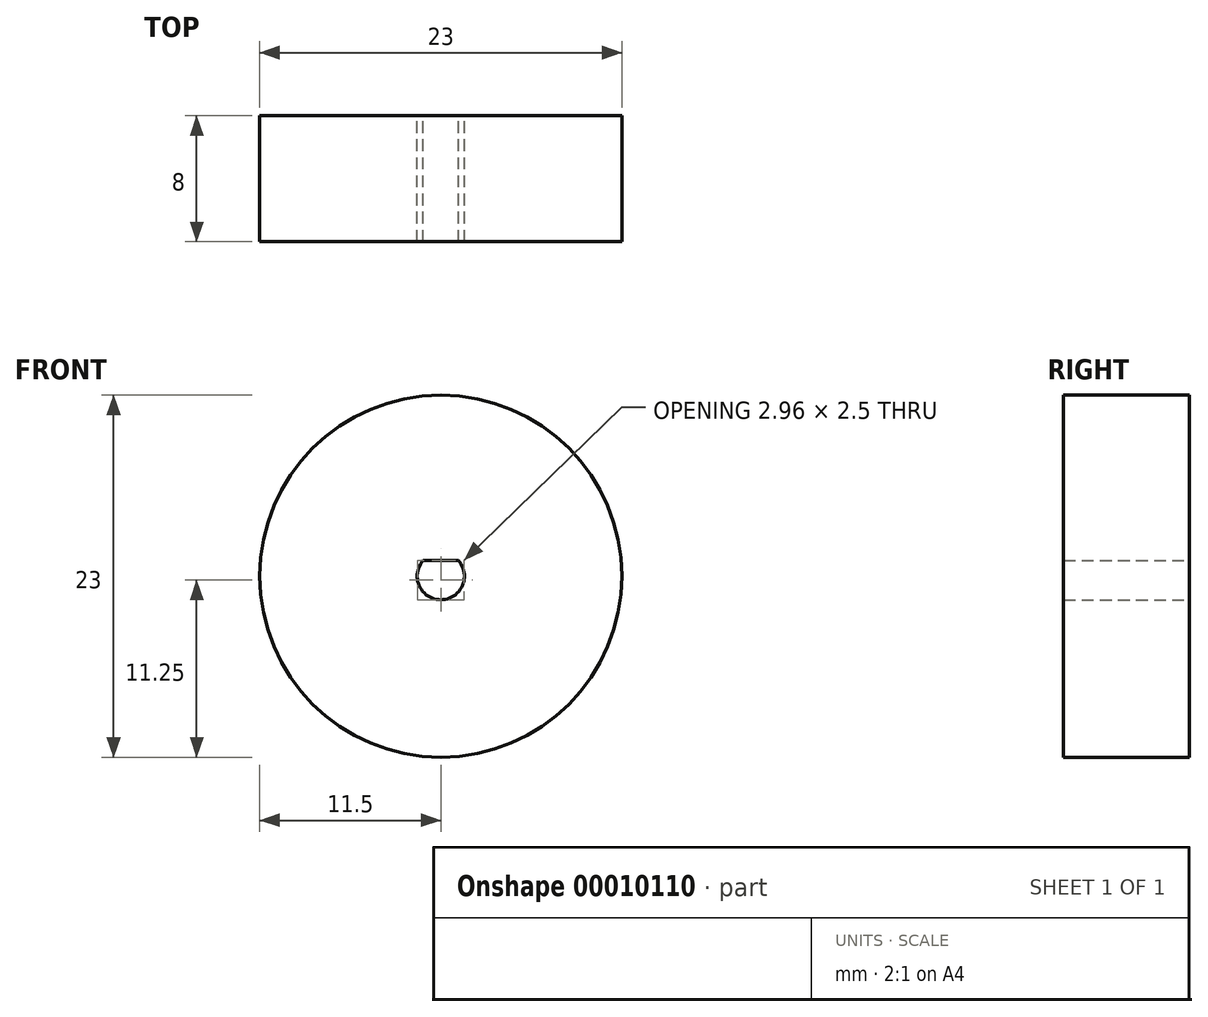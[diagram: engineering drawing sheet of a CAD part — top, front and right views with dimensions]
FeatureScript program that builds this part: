
annotation { "Feature Type Name" : "Feature", "Feature Type Description" : "" }
export const myFeature = defineFeature(function(context is Context, id is Id, definition is map)
    precondition{}
    {
        {
            var Q0;
            Q0=qCreatedBy(makeId("Front.planeOp"),FACE);
            var sketch = newSketch(context, id + "F0", { "sketchPlane" : qUnion([Q0])});
            skCircle(sketch, "E0", {"center": v(0, 0) * mm, "radius": 11.5 * mm});
            skArc(sketch, "E1", {"start": v(-1.12, 1) * mm, "mid": v(0, -1.5) * mm, "end": v(1.12, 1) * mm});
            skLineSegment(sketch, "E2", {"start": v(-1.12, 1) * mm, "end": v(1.12, 1) * mm});
            skSolve(sketch);
        }
        {
            var Q0;
            Q0 = qSketchRegion(id + "F0", true);
            extrude(context, id + "F1", {"entities" : qUnion([Q0]), "depth" : 8 * mm});
        }
    });
